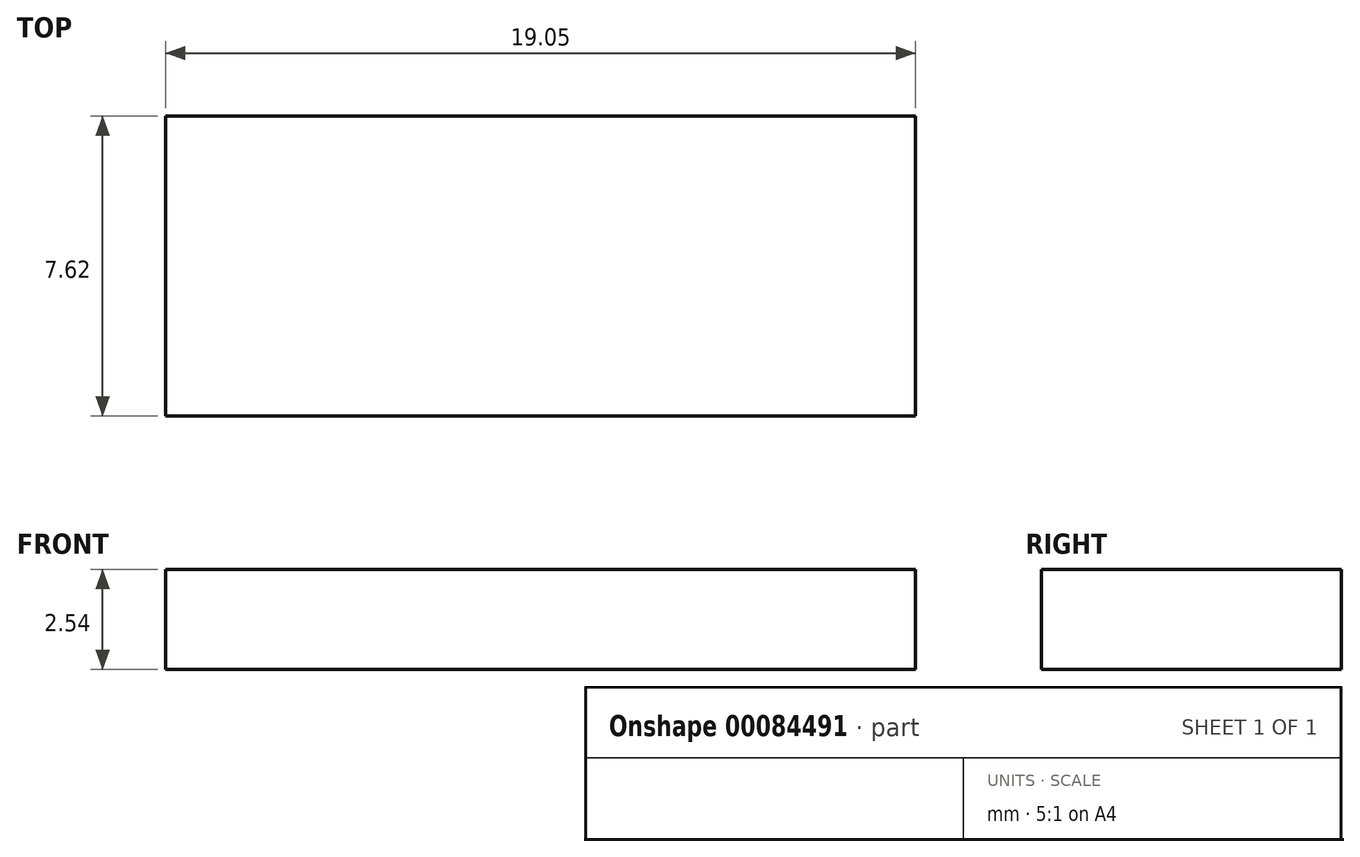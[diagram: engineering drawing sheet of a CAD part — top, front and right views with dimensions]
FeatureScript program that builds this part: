
annotation { "Feature Type Name" : "Feature", "Feature Type Description" : "" }
export const myFeature = defineFeature(function(context is Context, id is Id, definition is map)
    precondition{}
    {
        {
            var Q0;
            Q0=qCreatedBy(makeId("Top.planeOp"),FACE);
            var sketch = newSketch(context, id + "F0", { "sketchPlane" : qUnion([Q0])});
            skLineSegment(sketch, "E0.bottom", {"start": v(-65.48, 12.13) * mm, "end": v(-46.43, 12.13) * mm});
            skLineSegment(sketch, "E0.top", {"start": v(-65.48, 4.51) * mm, "end": v(-46.43, 4.51) * mm});
            skLineSegment(sketch, "E0.left", {"start": v(-65.48, 12.13) * mm, "end": v(-65.48, 4.51) * mm});
            skLineSegment(sketch, "E0.right", {"start": v(-46.43, 12.13) * mm, "end": v(-46.43, 4.51) * mm});
            skSolve(sketch);
        }
        {
            var Q0;
            Q0=makeQuery(id+"F0.imprint","IMPRINT",FACE,{"disambiguationData":[TD([[makeQuery(id+"F0.imprint","IMPRINT",EDGE,{"derivedFrom":sQuery(id+"F0.wireOp",EDGE,"E0.bottom")}),-1.0]])]});
            extrude(context, id + "F1", {"entities" : qUnion([Q0]), "depth" : 2.54 * mm});
        }
    });
